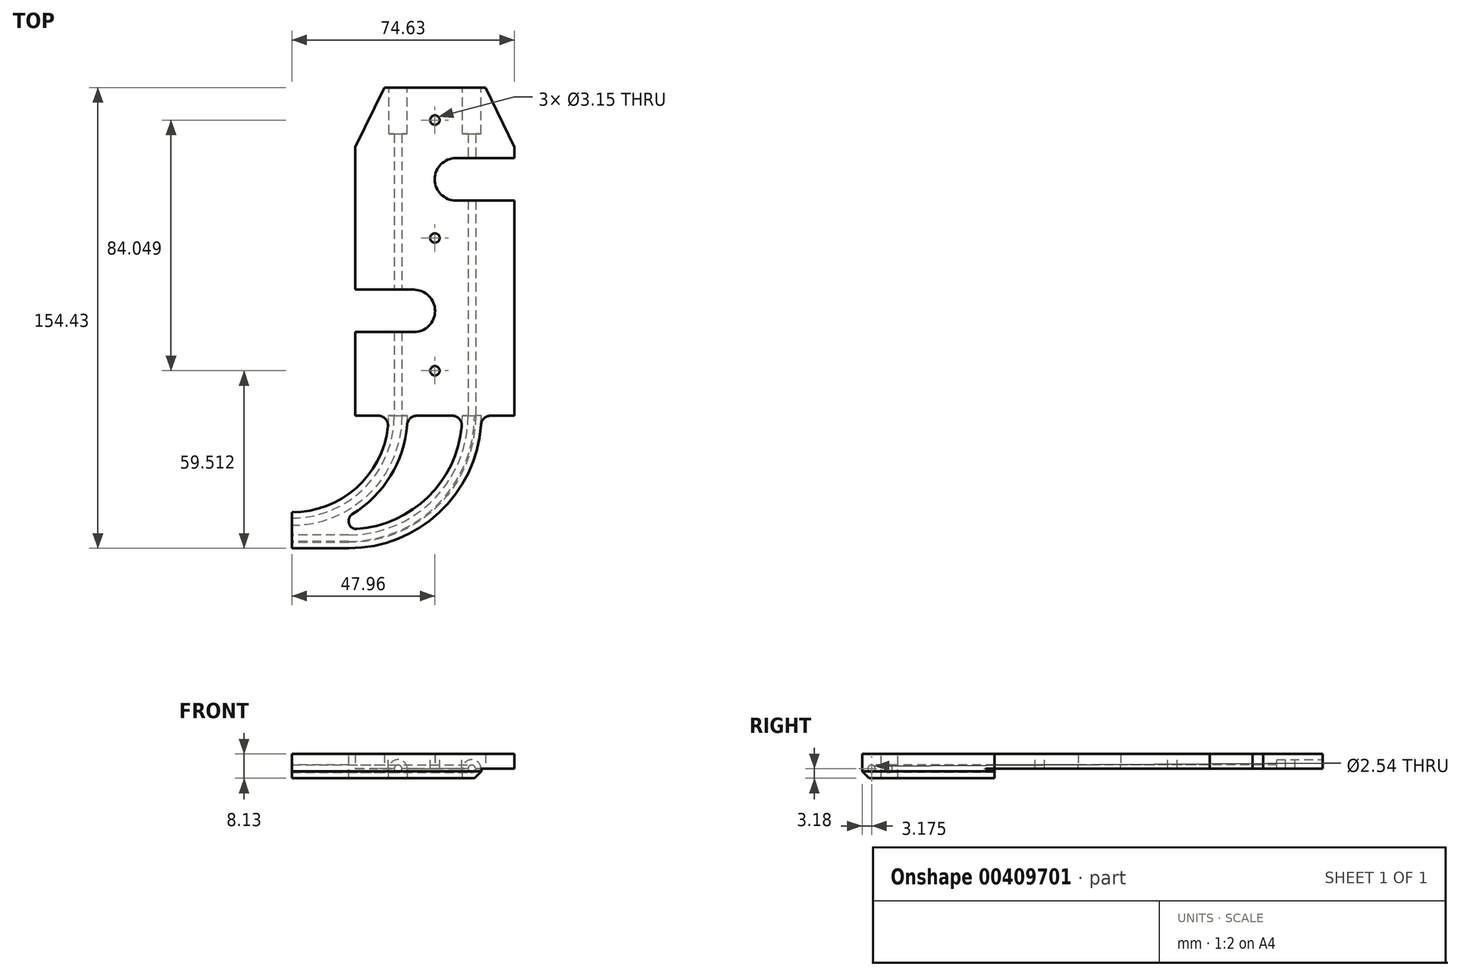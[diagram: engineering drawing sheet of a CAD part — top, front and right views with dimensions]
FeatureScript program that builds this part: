
annotation { "Feature Type Name" : "Feature", "Feature Type Description" : "" }
export const myFeature = defineFeature(function(context is Context, id is Id, definition is map)
    precondition{}
    {
        {
            var Q0;
            Q0=qCreatedBy(makeId("Top.planeOp"),FACE);
            var sketch = newSketch(context, id + "F0", { "sketchPlane" : qUnion([Q0])});
            skLineSegment(sketch, "E0", {"start": v(26.67, 0) * mm, "end": v(-26.67, 0) * mm});
            skLineSegment(sketch, "E1", {"start": v(-26.67, 0) * mm, "end": v(-26.67, 90.04) * mm});
            skLineSegment(sketch, "E2", {"start": v(-26.67, 90.04) * mm, "end": v(-16.94, 109.98) * mm});
            skLineSegment(sketch, "E3", {"start": v(-16.94, 109.98) * mm, "end": v(16.94, 109.98) * mm});
            skLineSegment(sketch, "E4", {"start": v(26.67, 0) * mm, "end": v(26.67, 90.04) * mm});
            skLineSegment(sketch, "E5", {"start": v(26.67, 90.04) * mm, "end": v(16.94, 109.98) * mm});
            skSolve(sketch);
        }
        {
            var Q0;
            Q0 = qSketchRegion(id + "F0", true);
            extrude(context, id + "F1", {"entities" : qUnion([Q0]), "depth" : 4.95 * mm});
        }
        {
            var Q0;
            Q0=qCreatedBy(makeId("Top.planeOp"),FACE);
            var sketch = newSketch(context, id + "F2", { "sketchPlane" : qUnion([Q0])});
            skLineSegment(sketch, "E6", {"start": v(-7.06, 28.02) * mm, "end": v(-26.67, 28.02) * mm});
            skLineSegment(sketch, "E7", {"start": v(-26.67, 28.02) * mm, "end": v(-26.67, 42.24) * mm});
            skLineSegment(sketch, "E8", {"start": v(-26.67, 42.24) * mm, "end": v(-7.06, 42.24) * mm});
            skArc(sketch, "E9", {"start": v(-7.06, 42.24) * mm, "mid": v(0.05, 35.13) * mm, "end": v(-7.06, 28.02) * mm});
            skLineSegment(sketch, "E10", {"start": v(-26.67, 42.24) * mm, "end": v(-26.67, 28.02) * mm});
            skLineSegment(sketch, "E11", {"start": v(7.06, 86.36) * mm, "end": v(26.67, 86.36) * mm});
            skLineSegment(sketch, "E12", {"start": v(26.67, 86.36) * mm, "end": v(26.67, 72.14) * mm});
            skLineSegment(sketch, "E13", {"start": v(26.67, 72.14) * mm, "end": v(7.06, 72.14) * mm});
            skArc(sketch, "E14", {"start": v(7.06, 86.36) * mm, "mid": v(-0.05, 79.25) * mm, "end": v(7.06, 72.14) * mm});
            skSolve(sketch);
        }
        {
            var Q0;
            Q0 = qSketchRegion(id + "F2", true);
            extrude(context, id + "F3", {"entities" : qUnion([Q0]), "operationType" : NewBodyOperationType.REMOVE, "endBound" : BoundingType.THROUGH_ALL, "depth" : 25.4 * mm});
        }
        {
            var Q0;
            Q0=makeQuery(id+"F1.opExtrude","SWEPT_FACE",FACE,{"disambiguationData":[OSD([sQuery(id+"F0.wireOp",EDGE,"E0")])]});
            var sketch = newSketch(context, id + "F4", { "sketchPlane" : qUnion([Q0])});
            skArc(sketch, "E15", {"start": v(-13.63, 0) * mm, "mid": v(-12.36, 1.27) * mm, "end": v(-11.09, 0) * mm});
            skArc(sketch, "E16", {"start": v(11.09, 0) * mm, "mid": v(12.36, 1.27) * mm, "end": v(13.63, 0) * mm});
            skLineSegment(sketch, "E17", {"start": v(-13.63, 0) * mm, "end": v(-11.09, 0) * mm});
            skLineSegment(sketch, "E18", {"start": v(11.09, 0) * mm, "end": v(13.63, 0) * mm});
            skLineSegment(sketch, "E19", {"start": v(-11.09, 0) * mm, "end": v(11.09, 0) * mm, "construction": true});
            skSolve(sketch);
        }
        {
            var Q0;
            Q0 = qSketchRegion(id + "F4", true);
            extrude(context, id + "F5", {"entities" : qUnion([Q0]), "operationType" : NewBodyOperationType.REMOVE, "endBound" : BoundingType.THROUGH_ALL, "oppositeDirection" : true, "depth" : 25.4 * mm});
        }
        {
            var Q0;
            Q0=makeQuery(id+"F1.opExtrude","SWEPT_FACE",FACE,{"disambiguationData":[OSD([sQuery(id+"F0.wireOp",EDGE,"E3")])]});
            var sketch = newSketch(context, id + "F6", { "sketchPlane" : qUnion([Q0])});
            skArc(sketch, "E20", {"start": v(-15.43, 0) * mm, "mid": v(-12.36, 3.07) * mm, "end": v(-9.28, 0) * mm});
            skArc(sketch, "E21", {"start": v(9.28, 0) * mm, "mid": v(12.36, 3.07) * mm, "end": v(15.43, 0) * mm});
            skLineSegment(sketch, "E22", {"start": v(-15.43, 0) * mm, "end": v(-9.28, 0) * mm});
            skLineSegment(sketch, "E23", {"start": v(9.28, 0) * mm, "end": v(15.43, 0) * mm});
            skSolve(sketch);
        }
        {
            var Q0;
            Q0 = qSketchRegion(id + "F6", true);
            extrude(context, id + "F7", {"entities" : qUnion([Q0]), "operationType" : NewBodyOperationType.REMOVE, "oppositeDirection" : true, "depth" : 15.5 * mm});
        }
        {
            var Q0;
            Q0=qCreatedBy(makeId("Top.planeOp"),FACE);
            var sketch = newSketch(context, id + "F8", { "sketchPlane" : qUnion([Q0])});
            skLineSegment(sketch, "E24.bottom", {"start": v(-47.96, 0) * mm, "end": v(26.67, 0) * mm});
            skLineSegment(sketch, "E24.top", {"start": v(-47.96, -44.45) * mm, "end": v(26.67, -44.45) * mm});
            skLineSegment(sketch, "E24.left", {"start": v(-47.96, 0) * mm, "end": v(-47.96, -44.45) * mm});
            skLineSegment(sketch, "E24.right", {"start": v(26.67, 0) * mm, "end": v(26.67, -44.45) * mm});
            skSolve(sketch);
        }
        {
            var Q0;
            Q0 = qSketchRegion(id + "F8", true);
            extrude(context, id + "F9", {"entities" : qUnion([Q0]), "operationType" : NewBodyOperationType.ADD, "depth" : 4.95 * mm, "hasSecondDirection" : true, "secondDirectionOppositeDirection" : true, "secondDirectionDepth" : 3.17 * mm});
        }
        {
            var Q0;
            Q0=qCreatedBy(makeId("Top.planeOp"),FACE);
            var sketch = newSketch(context, id + "F10", { "sketchPlane" : qUnion([Q0])});
            skLineSegment(sketch, "E25", {"start": v(-28.92, 0) * mm, "end": v(-28.92, -41.28) * mm, "construction": true});
            skLineSegment(sketch, "E26", {"start": v(-47.96, -41.28) * mm, "end": v(-28.92, -41.28) * mm});
            skLineSegment(sketch, "E27", {"start": v(11.09, 0) * mm, "end": v(13.63, 0) * mm, "construction": true});
            skArc(sketch, "E28", {"start": v(12.36, 0) * mm, "mid": v(0.27, -29.19) * mm, "end": v(-28.92, -41.28) * mm});
            skSolve(sketch);
        }
        {
            var Q0;
            Q0=makeQuery(id+"F9.opExtrude","SWEPT_FACE",FACE,{"disambiguationData":[OSD([sQuery(id+"F8.wireOp",EDGE,"E24.bottom")])]});
            var sketch = newSketch(context, id + "F11", { "sketchPlane" : qUnion([Q0])});
            skCircle(sketch, "E29", {"center": v(-12.36, 0) * mm, "radius": 1.27 * mm});
            skSolve(sketch);
        }
        {
            var Q0;
            Q0 = qSketchRegion(id + "F11", true);
            var Q1;
            Q1 = qConstructionFilter(qBodyType(qCreatedBy(id + "F10" ,EDGE), BodyType.WIRE), ConstructionObject.NO);
            sweep(context, id + "F12", {"operationType" : NewBodyOperationType.REMOVE, "profiles" : qUnion([Q0]), "path" : qUnion([Q1])});
        }
        {
            var Q0;
            Q0=qCreatedBy(makeId("Top.planeOp"),FACE);
            var sketch = newSketch(context, id + "F13", { "sketchPlane" : qUnion([Q0])});
            skLineSegment(sketch, "E30", {"start": v(-13.63, 0) * mm, "end": v(-11.09, 0) * mm, "construction": true});
            skArc(sketch, "E31", {"start": v(-12.36, 0) * mm, "mid": v(-22.78, -25.17) * mm, "end": v(-47.96, -35.6) * mm});
            skSolve(sketch);
        }
        {
            var Q0;
            Q0=makeQuery(id+"F9.opExtrude","SWEPT_FACE",FACE,{"disambiguationData":[OSD([sQuery(id+"F8.wireOp",EDGE,"E24.bottom")])]});
            var sketch = newSketch(context, id + "F14", { "sketchPlane" : qUnion([Q0])});
            skCircle(sketch, "E32", {"center": v(12.36, 0) * mm, "radius": 1.27 * mm});
            skSolve(sketch);
        }
        {
            var Q0;
            {var subQ0=sQuery(id+"F14.wireOp",EDGE,"E32");var subQ1=sQuery(id+"F0.wireOp",EDGE,"E0");var subQ2=makeQuery(id+"F1.opExtrude","SWEPT_FACE",FACE,{"disambiguationData":[OSD([subQ1])]});var subQ3=makeQuery(id+"F5.opExtrude","SWEPT_FACE",FACE,{"disambiguationData":[OSD([sQuery(id+"F4.wireOp",EDGE,"E16")])]});var subQ4=sQuery(id+"F0.wireOp",EDGE,"E4");var subQ5=makeQuery(id+"F1.opExtrude","CAP_FACE",FACE,{"disambiguationData":[OSD([subQ1,sQuery(id+"F0.wireOp",EDGE,"E1"),sQuery(id+"F0.wireOp",EDGE,"E2"),sQuery(id+"F0.wireOp",EDGE,"E3"),subQ4,sQuery(id+"F0.wireOp",EDGE,"E5")])],"isStart":true});var subQ6=makeQuery(id+"F1.opExtrude","CAP_EDGE",EDGE,{"disambiguationData":[OSD([subQ1])],"isStart":true});var subQ7=makeQuery(id+"F14.imprint","INTERSECT",VERTEX,{"derivedFrom":[makeQuery(id+"F5.boolean.opBoolean","SPLIT",EDGE,{"disambiguationData":[TD([subQ2,subQ5,makeQuery(id+"F5.opExtrude","SWEPT_FACE",FACE,{"disambiguationData":[OSD([sQuery(id+"F4.wireOp",EDGE,"E15")])]}),subQ3])],"derivedFrom":subQ6}),subQ0]});Q0=makeQuery(id+"F14.imprint","IMPRINT",FACE,{"disambiguationData":[TD([[makeQuery(id+"F14.imprint","IMPRINT",EDGE,{"disambiguationData":[TD([[subQ7,-1.0]])],"derivedFrom":subQ0}),1.0]])]});}
            var Q1;
            Q1 = qConstructionFilter(qBodyType(qCreatedBy(id + "F13" ,EDGE), BodyType.WIRE), ConstructionObject.NO);
            sweep(context, id + "F15", {"operationType" : NewBodyOperationType.REMOVE, "profiles" : qUnion([Q0]), "path" : qUnion([Q1])});
        }
        {
            var Q0;
            Q0=qCreatedBy(makeId("Top.planeOp"),FACE);
            var sketch = newSketch(context, id + "F16", { "sketchPlane" : qUnion([Q0])});
            skLineSegment(sketch, "E33", {"start": v(26.67, -44.45) * mm, "end": v(-28.92, -44.45) * mm});
            skLineSegment(sketch, "E34", {"start": v(15.53, 0) * mm, "end": v(26.67, 0) * mm});
            skArc(sketch, "E35", {"start": v(15.53, 0) * mm, "mid": v(2.51, -31.43) * mm, "end": v(-28.92, -44.45) * mm});
            skArc(sketch, "E36", {"start": v(9.18, 0) * mm, "mid": v(-1.98, -26.94) * mm, "end": v(-28.92, -38.1) * mm});
            skArc(sketch, "E37", {"start": v(-15.53, 0) * mm, "mid": v(-25.03, -22.93) * mm, "end": v(-47.96, -32.42) * mm});
            skLineSegment(sketch, "E38", {"start": v(-28.92, 0) * mm, "end": v(-28.92, 0) * mm});
            skLineSegment(sketch, "E39", {"start": v(-47.96, -32.42) * mm, "end": v(-47.96, 0) * mm});
            skLineSegment(sketch, "E40", {"start": v(-15.53, 0) * mm, "end": v(-9.18, 0) * mm, "construction": true});
            skLineSegment(sketch, "E41", {"start": v(9.18, 0) * mm, "end": v(15.53, 0) * mm, "construction": true});
            skLineSegment(sketch, "E42", {"start": v(-15.53, 0) * mm, "end": v(-47.96, 0) * mm});
            skLineSegment(sketch, "E43", {"start": v(-9.18, 0) * mm, "end": v(9.18, 0) * mm});
            skArc(sketch, "E44", {"start": v(-9.18, 0) * mm, "mid": v(-14.47, -19.54) * mm, "end": v(-28.88, -33.75) * mm});
            skLineSegment(sketch, "E45", {"start": v(-28.92, -38.1) * mm, "end": v(-28.88, -33.75) * mm});
            skLineSegment(sketch, "E46", {"start": v(26.67, -44.45) * mm, "end": v(26.67, 0) * mm});
            skSolve(sketch);
        }
        {
            var Q0;
            Q0 = qSketchRegion(id + "F16", true);
            extrude(context, id + "F17", {"entities" : qUnion([Q0]), "operationType" : NewBodyOperationType.REMOVE, "endBound" : BoundingType.THROUGH_ALL, "oppositeDirection" : true, "depth" : 25.4 * mm, "hasSecondDirection" : true, "secondDirectionBound" : SecondDirectionBoundingType.THROUGH_ALL, "secondDirectionOppositeDirection" : false, "secondDirectionDepth" : 25.4 * mm});
        }
        {
            var Q0;
            Q0=makeQuery(id+"F9.boolean.opBoolean","MERGE",FACE,{"derivedFrom":[makeQuery(id+"F1.opExtrude","CAP_FACE",FACE,{"disambiguationData":[OSD([sQuery(id+"F0.wireOp",EDGE,"E0"),sQuery(id+"F0.wireOp",EDGE,"E1"),sQuery(id+"F0.wireOp",EDGE,"E2"),sQuery(id+"F0.wireOp",EDGE,"E3"),sQuery(id+"F0.wireOp",EDGE,"E4"),sQuery(id+"F0.wireOp",EDGE,"E5")])],"isStart":false}),makeQuery(id+"F9.opExtrude","CAP_FACE",FACE,{"disambiguationData":[OSD([sQuery(id+"F8.wireOp",EDGE,"E24.bottom"),sQuery(id+"F8.wireOp",EDGE,"E24.top"),sQuery(id+"F8.wireOp",EDGE,"E24.left"),sQuery(id+"F8.wireOp",EDGE,"E24.right")])],"isStart":false})]});
            var sketch = newSketch(context, id + "F18", { "sketchPlane" : qUnion([Q0])});
            skPoint(sketch, "E47", {"position": v(0, 99.11) * mm});
            skPoint(sketch, "E48", {"position": v(0, 59.56) * mm});
            skPoint(sketch, "E49", {"position": v(0, 15.06) * mm});
            skSolve(sketch);
        }
        {
            var Q0;
            Q0=sQuery(id+"F18.wireOp",VERTEX,"E47");
            var Q1;
            Q1=sQuery(id+"F18.wireOp",VERTEX,"E48");
            var Q2;
            Q2=sQuery(id+"F18.wireOp",VERTEX,"E49");
            var Q3;
            Q3=makeQuery(id+"F1.opExtrude","SWEPT_BODY",BODY,{"disambiguationData":[OSD([sQuery(id+"F0.wireOp",EDGE,"E0"),sQuery(id+"F0.wireOp",EDGE,"E1"),sQuery(id+"F0.wireOp",EDGE,"E2"),sQuery(id+"F0.wireOp",EDGE,"E3"),sQuery(id+"F0.wireOp",EDGE,"E4"),sQuery(id+"F0.wireOp",EDGE,"E5")])]});
            hole(context, id + "F19", {"style" : HoleStyle.SIMPLE, "endStyle" : HoleEndStyle.THROUGH, "standardTappedOrClearance" : lookupTablePath({ "standard" : "ISO", "fit" : "Close", "size" : "M3", "type" : "Clearance" }), "standardBlindInLast" : lookupTablePath({ "fit" : "Close", "standard" : "ISO", "size" : "M3", "type" : "Clearance" }), "holeDiameter" : 3.15 * mm, "isTappedThrough" : true, "tappedDepth" : 12.7 * mm, "tapClearance" : 3, "locations" : qUnion([Q0, Q1, Q2]), "scope" : qUnion([Q3])});
        }
        {
            var Q0;
            {var subQ0=sQuery(id+"F16.wireOp",EDGE,"E36");var subQ1=sQuery(id+"F16.wireOp",EDGE,"E43");Q0=makeQuery(id+"F17.boolean.opBoolean","COPY",EDGE,{"disambiguationData":[topologyDisambiguationEdgeConnected([makeQuery(id+"F17.opExtrude","SWEPT_FACE",FACE,{"disambiguationData":[OSD([subQ1])]})])],"derivedFrom":makeQuery(id+"F17.opExtrude","SWEPT_EDGE",EDGE,{"disambiguationData":[OSD([subQ0,subQ1])]})});}
            var Q1;
            {var subQ0=sQuery(id+"F16.wireOp",EDGE,"E43");var subQ1=sQuery(id+"F16.wireOp",EDGE,"E44");Q1=makeQuery(id+"F17.boolean.opBoolean","COPY",EDGE,{"disambiguationData":[topologyDisambiguationEdgeConnected([makeQuery(id+"F17.opExtrude","SWEPT_FACE",FACE,{"disambiguationData":[OSD([subQ0])]})])],"derivedFrom":makeQuery(id+"F17.opExtrude","SWEPT_EDGE",EDGE,{"disambiguationData":[OSD([subQ0,subQ1])]})});}
            var Q2;
            {var subQ0=sQuery(id+"F16.wireOp",EDGE,"E34");var subQ1=sQuery(id+"F16.wireOp",EDGE,"E35");Q2=makeQuery(id+"F17.boolean.opBoolean","COPY",EDGE,{"disambiguationData":[topologyDisambiguationEdgeConnected([makeQuery(id+"F17.opExtrude","SWEPT_FACE",FACE,{"disambiguationData":[OSD([subQ0])]})])],"derivedFrom":makeQuery(id+"F17.opExtrude","SWEPT_EDGE",EDGE,{"disambiguationData":[OSD([subQ0,subQ1])]})});}
            var Q3;
            {var subQ0=sQuery(id+"F16.wireOp",EDGE,"E37");var subQ1=sQuery(id+"F16.wireOp",EDGE,"E42");Q3=makeQuery(id+"F17.boolean.opBoolean","COPY",EDGE,{"disambiguationData":[topologyDisambiguationEdgeConnected([makeQuery(id+"F17.opExtrude","SWEPT_FACE",FACE,{"disambiguationData":[OSD([subQ1])]})])],"derivedFrom":makeQuery(id+"F17.opExtrude","SWEPT_EDGE",EDGE,{"disambiguationData":[OSD([subQ0,subQ1])]})});}
            fillet(context, id + "F20", {"entities" : qUnion([Q0, Q1, Q2, Q3]), "radius" : 3.3 * mm, "tangentPropagation" : true, "allowEdgeOverflow" : false});
        }
        {
            var Q0;
            Q0=makeQuery(id+"F17.boolean.opBoolean","COPY",EDGE,{"derivedFrom":makeQuery(id+"F17.opExtrude","SWEPT_EDGE",EDGE,{"disambiguationData":[OSD([sQuery(id+"F16.wireOp",EDGE,"E44"),sQuery(id+"F16.wireOp",EDGE,"E45")])]})});
            var Q1;
            Q1=makeQuery(id+"F17.boolean.opBoolean","COPY",EDGE,{"derivedFrom":makeQuery(id+"F17.opExtrude","SWEPT_EDGE",EDGE,{"disambiguationData":[OSD([sQuery(id+"F16.wireOp",EDGE,"E36"),sQuery(id+"F16.wireOp",EDGE,"E45")])]})});
            fillet(context, id + "F21", {"entities" : qUnion([Q0, Q1]), "radius" : 2.54 * mm, "tangentPropagation" : true, "allowEdgeOverflow" : false});
        }
        {
            var Q0;
            Q0=makeQuery(id+"F17.boolean.opBoolean","INTERSECT",EDGE,{"derivedFrom":[makeQuery(id+"F9.opExtrude","CAP_FACE",FACE,{"disambiguationData":[OSD([sQuery(id+"F8.wireOp",EDGE,"E24.bottom"),sQuery(id+"F8.wireOp",EDGE,"E24.top"),sQuery(id+"F8.wireOp",EDGE,"E24.left"),sQuery(id+"F8.wireOp",EDGE,"E24.right")])],"isStart":true}),makeQuery(id+"F17.opExtrude","SWEPT_FACE",FACE,{"disambiguationData":[OSD([sQuery(id+"F16.wireOp",EDGE,"UKAjmSGH-oJ1n-svVJ-Vxux-B9e3HcnW0MhH")])]})]});
            var Q1;
            Q1=makeQuery(id+"F17.boolean.opBoolean","INTERSECT",EDGE,{"derivedFrom":[makeQuery(id+"F9.opExtrude","CAP_FACE",FACE,{"disambiguationData":[OSD([sQuery(id+"F8.wireOp",EDGE,"E24.bottom"),sQuery(id+"F8.wireOp",EDGE,"E24.top"),sQuery(id+"F8.wireOp",EDGE,"E24.left"),sQuery(id+"F8.wireOp",EDGE,"E24.right")])],"isStart":true}),makeQuery(id+"F17.opExtrude","SWEPT_FACE",FACE,{"disambiguationData":[OSD([sQuery(id+"F16.wireOp",EDGE,"9wG90Vpw-plPm-8BCo-CBiY-iTRwfduYAdga")])]})]});
            var Q2;
            Q2=makeQuery(id+"F9.opExtrude","CAP_EDGE",EDGE,{"disambiguationData":[OSD([sQuery(id+"F8.wireOp",EDGE,"E24.top")])],"isStart":true});
            var Q3;
            Q3=makeQuery(id+"F9.opExtrude","CAP_EDGE",EDGE,{"disambiguationData":[OSD([sQuery(id+"F8.wireOp",EDGE,"E24.right")])],"isStart":true});
            chamfer(context, id + "F22", {"entities" : qUnion([Q0, Q1, Q2, Q3]), "width" : 2.3 * mm, "tangentPropagation" : true});
        }
    });
